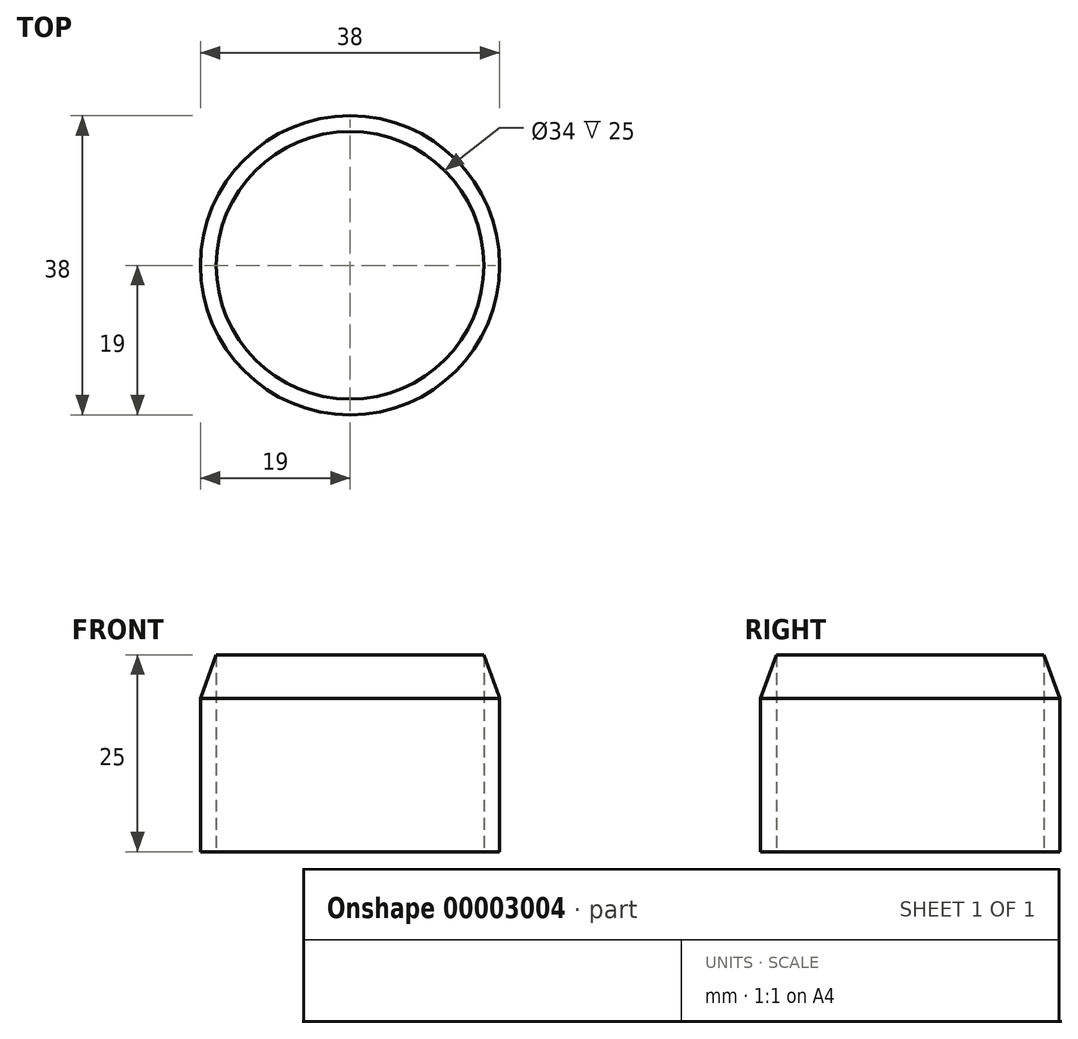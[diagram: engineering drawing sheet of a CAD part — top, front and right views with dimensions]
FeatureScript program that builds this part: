
annotation { "Feature Type Name" : "Feature", "Feature Type Description" : "" }
export const myFeature = defineFeature(function(context is Context, id is Id, definition is map)
    precondition{}
    {
        {
            var Q0;
            Q0=qCreatedBy(makeId("Top.planeOp"),FACE);
            var sketch = newSketch(context, id + "F0", { "sketchPlane" : qUnion([Q0])});
            skCircle(sketch, "E0", {"center": v(0, 0) * mm, "radius": 17 * mm});
            skCircle(sketch, "E1", {"center": v(0, 0) * mm, "radius": 19 * mm});
            skSolve(sketch);
        }
        {
            var Q0;
            Q0=makeQuery(id+"F0.imprint","IMPRINT",FACE,{"disambiguationData":[TD([[makeQuery(id+"F0.imprint","IMPRINT",EDGE,{"derivedFrom":sQuery(id+"F0.wireOp",EDGE,"E0")}),-1.0]])]});
            extrude(context, id + "F1", {"entities" : qUnion([Q0]), "depth" : 25 * mm});
        }
        {
            var Q0;
            Q0=makeQuery(id+"F1.opExtrude","CAP_EDGE",EDGE,{"disambiguationData":[OSD([sQuery(id+"F0.wireOp",EDGE,"E1")])],"isStart":false});
            chamfer(context, id + "F2", {"entities" : qUnion([Q0]), "chamferType" : ChamferType.OFFSET_ANGLE, "width" : 2 * mm, "oppositeDirection" : false, "angle" : 70 * degree, "tangentPropagation" : true});
        }
    });
